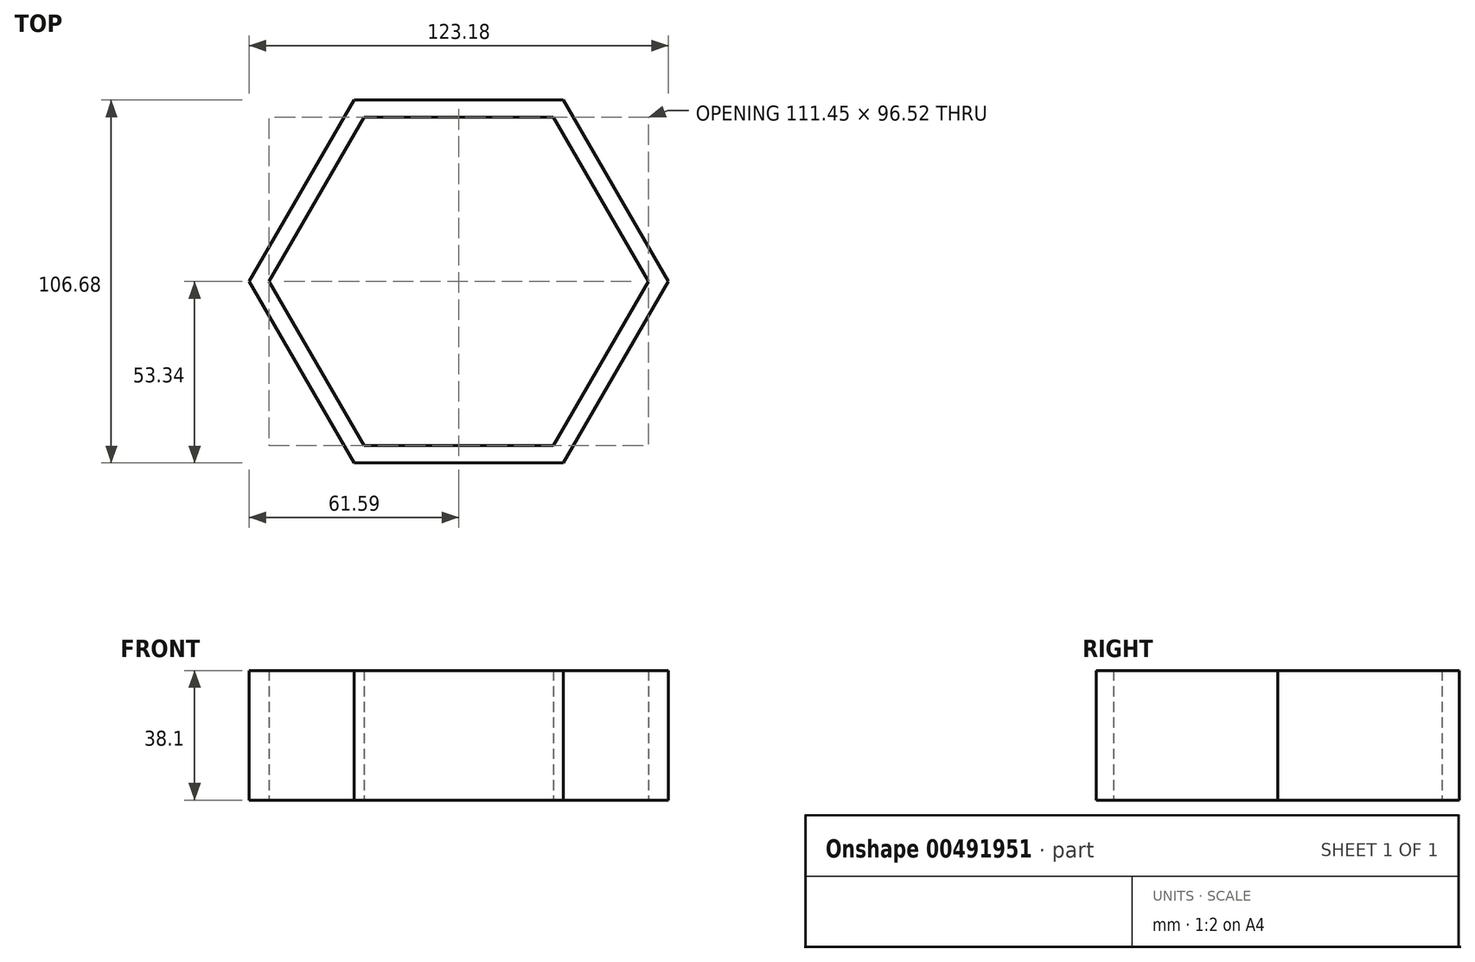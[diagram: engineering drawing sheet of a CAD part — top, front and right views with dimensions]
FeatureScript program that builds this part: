
annotation { "Feature Type Name" : "Feature", "Feature Type Description" : "" }
export const myFeature = defineFeature(function(context is Context, id is Id, definition is map)
    precondition{}
    {
        {
            var Q0;
            Q0=qCreatedBy(makeId("Top.planeOp"),FACE);
            var sketch = newSketch(context, id + "F0", { "sketchPlane" : qUnion([Q0])});
            skCircle(sketch, "E0.cCircle", {"center": v(0, 0) * mm, "radius": 53.34 * mm, "construction": true});
            skLineSegment(sketch, "E0.0", {"start": v(30.8, -53.34) * mm, "end": v(-30.8, -53.34) * mm});
            skLineSegment(sketch, "E0.1", {"start": v(-30.8, -53.34) * mm, "end": v(-61.6, 0) * mm});
            skLineSegment(sketch, "E0.2", {"start": v(-61.6, 0) * mm, "end": v(-30.8, 53.34) * mm});
            skLineSegment(sketch, "E0.3", {"start": v(-30.8, 53.34) * mm, "end": v(30.8, 53.34) * mm});
            skLineSegment(sketch, "E0.4", {"start": v(30.8, 53.34) * mm, "end": v(61.6, 0) * mm});
            skLineSegment(sketch, "E0.5", {"start": v(61.6, 0) * mm, "end": v(30.8, -53.34) * mm});
            skPoint(sketch, "E0.0.midPoint", {"position": v(0, -53.34) * mm});
            skLineSegment(sketch, "E1.0", {"start": v(-55.73, 0) * mm, "end": v(-27.86, 48.26) * mm});
            skLineSegment(sketch, "E1.1", {"start": v(27.86, 48.26) * mm, "end": v(55.73, 0) * mm});
            skLineSegment(sketch, "E1.2", {"start": v(55.73, 0) * mm, "end": v(27.86, -48.26) * mm});
            skLineSegment(sketch, "E1.3", {"start": v(-27.86, 48.26) * mm, "end": v(27.86, 48.26) * mm});
            skLineSegment(sketch, "E1.4", {"start": v(27.86, -48.26) * mm, "end": v(-27.86, -48.26) * mm});
            skLineSegment(sketch, "E1.5", {"start": v(-27.86, -48.26) * mm, "end": v(-55.73, 0) * mm});
            skSolve(sketch);
        }
        {
            var Q0;
            Q0 = qSketchRegion(id + "F0", true);
            extrude(context, id + "F1", {"entities" : qUnion([Q0]), "depth" : 38.1 * mm});
        }
    });
